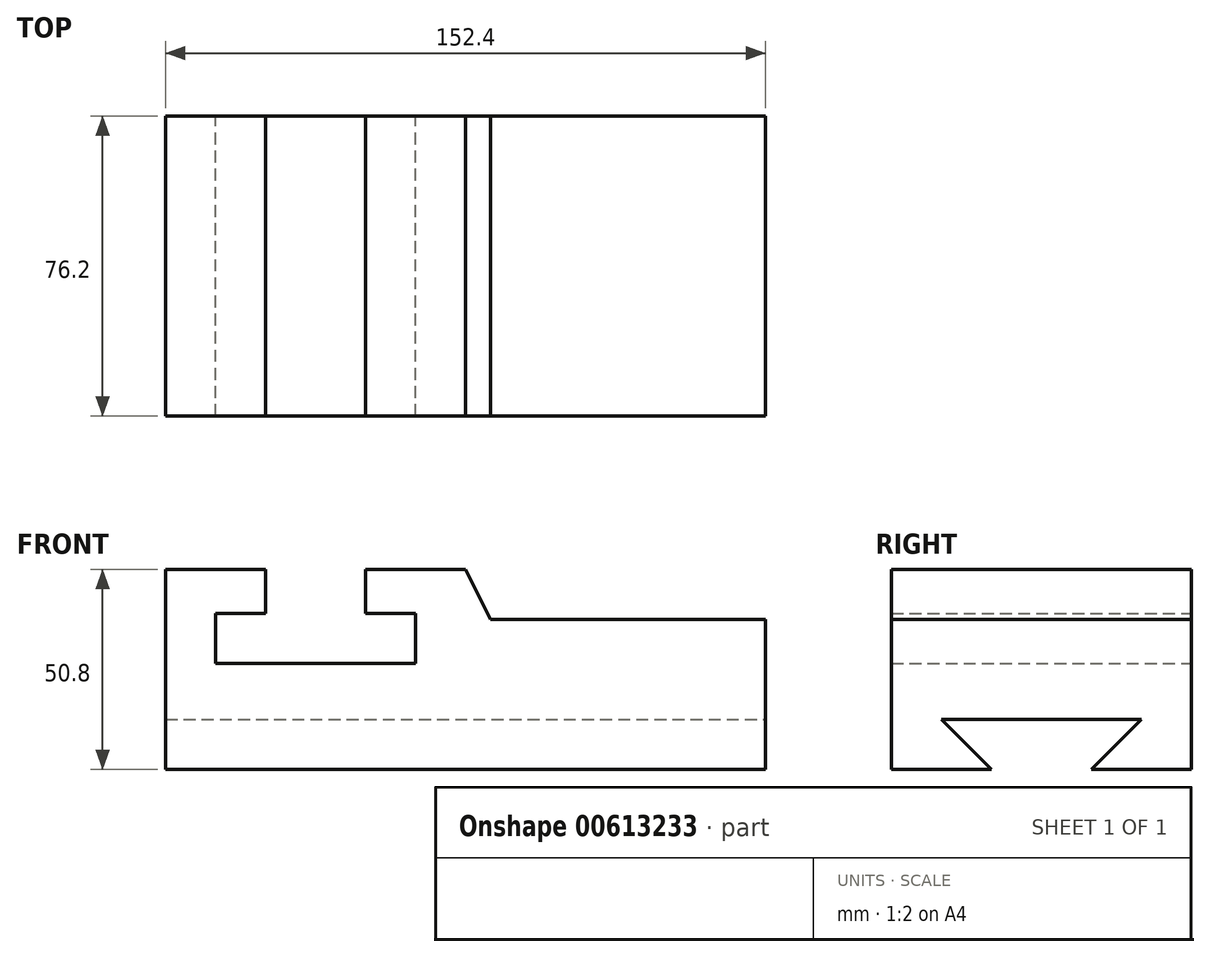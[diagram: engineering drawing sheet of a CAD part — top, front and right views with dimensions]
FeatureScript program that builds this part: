
annotation { "Feature Type Name" : "Feature", "Feature Type Description" : "" }
export const myFeature = defineFeature(function(context is Context, id is Id, definition is map)
    precondition{}
    {
        {
            var Q0;
            Q0=qCreatedBy(makeId("Front.planeOp"),FACE);
            var sketch = newSketch(context, id + "F0", { "sketchPlane" : qUnion([Q0])});
            skLineSegment(sketch, "E0", {"start": v(0, 0) * mm, "end": v(152.4, 0) * mm});
            skLineSegment(sketch, "E1", {"start": v(152.4, 0) * mm, "end": v(152.4, 38.1) * mm});
            skLineSegment(sketch, "E2", {"start": v(152.4, 38.1) * mm, "end": v(82.55, 38.1) * mm});
            skLineSegment(sketch, "E3", {"start": v(0, 0) * mm, "end": v(0, 50.8) * mm});
            skLineSegment(sketch, "E4", {"start": v(0, 50.8) * mm, "end": v(25.4, 50.8) * mm});
            skLineSegment(sketch, "E5", {"start": v(25.4, 50.8) * mm, "end": v(25.4, 39.68) * mm});
            skLineSegment(sketch, "E6", {"start": v(25.4, 39.68) * mm, "end": v(12.7, 39.68) * mm});
            skLineSegment(sketch, "E7", {"start": v(12.7, 39.68) * mm, "end": v(12.7, 26.98) * mm});
            skLineSegment(sketch, "E8", {"start": v(12.7, 26.98) * mm, "end": v(63.5, 26.98) * mm});
            skLineSegment(sketch, "E9", {"start": v(63.5, 26.98) * mm, "end": v(63.5, 39.68) * mm});
            skLineSegment(sketch, "E10", {"start": v(63.5, 39.68) * mm, "end": v(50.8, 39.68) * mm});
            skLineSegment(sketch, "E11", {"start": v(50.8, 39.68) * mm, "end": v(50.8, 50.8) * mm});
            skLineSegment(sketch, "E12", {"start": v(50.8, 50.8) * mm, "end": v(76.2, 50.8) * mm});
            skLineSegment(sketch, "E13", {"start": v(76.2, 50.8) * mm, "end": v(82.55, 38.1) * mm});
            skSolve(sketch);
        }
        {
            var Q0;
            Q0=makeQuery(id+"F0.imprint","IMPRINT",FACE,{"disambiguationData":[TD([[makeQuery(id+"F0.imprint","IMPRINT",EDGE,{"derivedFrom":sQuery(id+"F0.wireOp",EDGE,"E0")}),1.0]])]});
            extrude(context, id + "F1", {"entities" : qUnion([Q0]), "depth" : 76.2 * mm, "offsetDistance" : 25.4 * mm});
        }
        {
            var Q0;
            Q0=makeQuery(id+"F1.opExtrude","SWEPT_FACE",FACE,{"disambiguationData":[OSD([sQuery(id+"F0.wireOp",EDGE,"E1")])]});
            var sketch = newSketch(context, id + "F2", { "sketchPlane" : qUnion([Q0])});
            skLineSegment(sketch, "E14", {"start": v(-38.1, 12.7) * mm, "end": v(-63.5, 12.7) * mm});
            skLineSegment(sketch, "E15", {"start": v(-38.1, 12.7) * mm, "end": v(-12.7, 12.7) * mm});
            skLineSegment(sketch, "E16", {"start": v(-50.8, 0) * mm, "end": v(-63.5, 12.7) * mm});
            skLineSegment(sketch, "E17", {"start": v(-25.4, 0) * mm, "end": v(-12.7, 12.7) * mm});
            skSolve(sketch);
        }
        {
            var Q0;
            Q0=makeQuery(id+"F2.imprint","IMPRINT",FACE,{"disambiguationData":[TD([[makeQuery(id+"F2.imprint","IMPRINT",EDGE,{"derivedFrom":sQuery(id+"F2.wireOp",EDGE,"E14")}),1.0]])]});
            extrude(context, id + "F3", {"entities" : qUnion([Q0]), "operationType" : NewBodyOperationType.REMOVE, "endBound" : BoundingType.UP_TO_NEXT, "oppositeDirection" : true, "depth" : 25.4 * mm, "offsetDistance" : 25.4 * mm});
        }
    });
